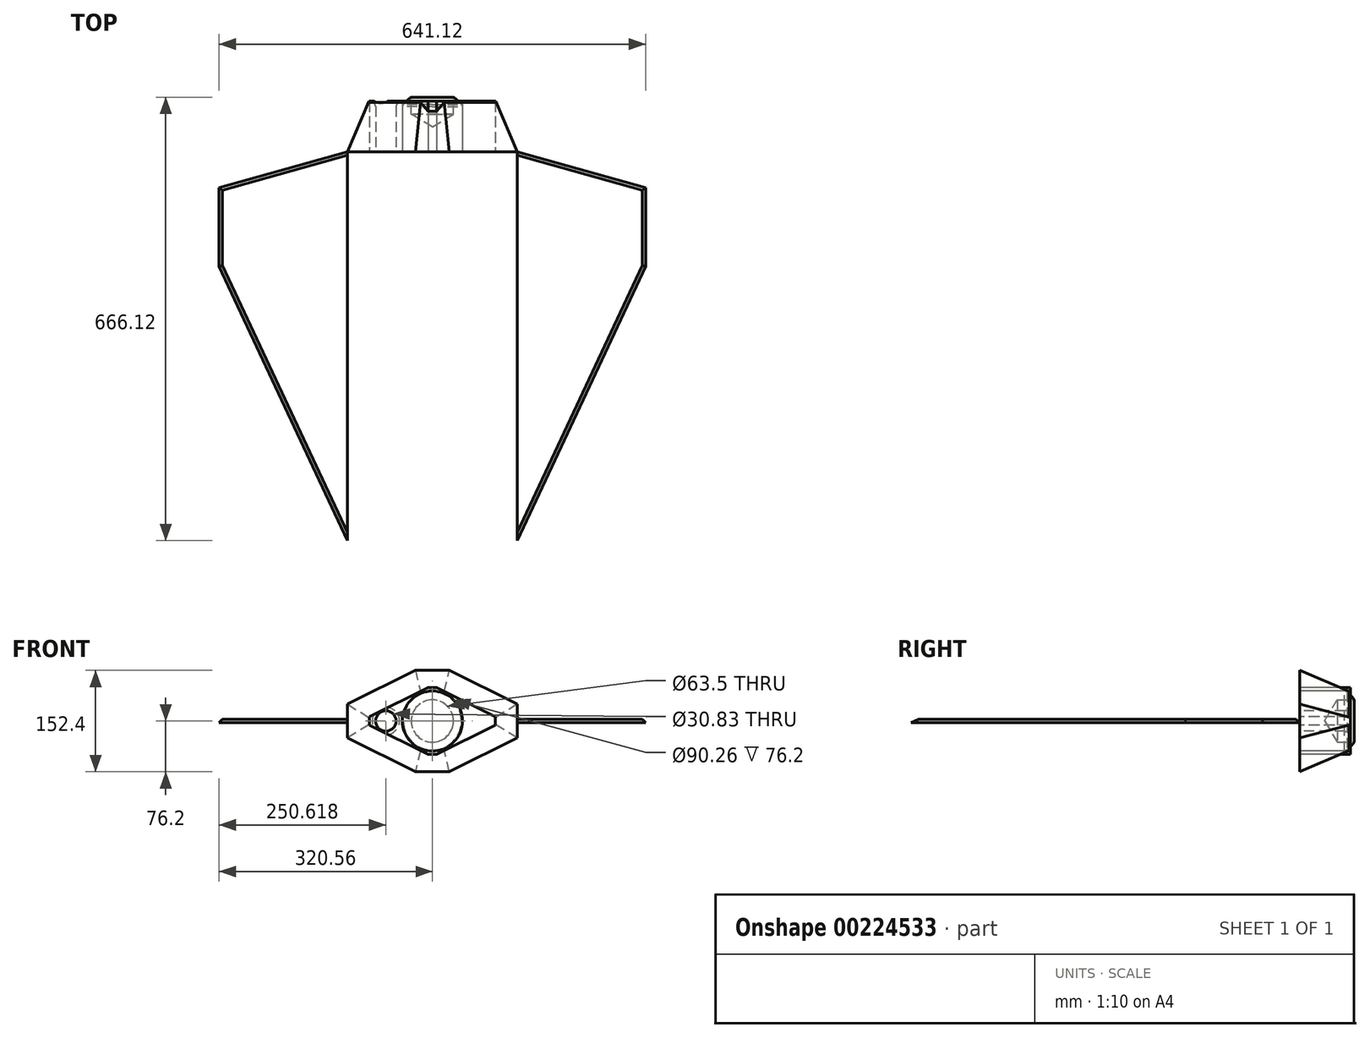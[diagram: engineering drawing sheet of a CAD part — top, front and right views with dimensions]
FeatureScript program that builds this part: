
annotation { "Feature Type Name" : "Feature", "Feature Type Description" : "" }
export const myFeature = defineFeature(function(context is Context, id is Id, definition is map)
    precondition{}
    {
        {
            var Q0;
            Q0=qCreatedBy(makeId("Top.planeOp"),FACE);
            var sketch = newSketch(context, id + "F0", { "sketchPlane" : qUnion([Q0])});
            skLineSegment(sketch, "E0", {"start": v(0, 0) * mm, "end": v(-127.58, 0) * mm});
            skLineSegment(sketch, "E1", {"start": v(0, 0) * mm, "end": v(0, -584.2) * mm});
            skLineSegment(sketch, "E2", {"start": v(0, -584.2) * mm, "end": v(-127.58, -584.2) * mm});
            skLineSegment(sketch, "E3", {"start": v(-127.58, -584.2) * mm, "end": v(-127.58, 0) * mm});
            skLineSegment(sketch, "E4", {"start": v(0, -584.2) * mm, "end": v(127.58, -584.2) * mm});
            skLineSegment(sketch, "E5", {"start": v(127.58, -584.2) * mm, "end": v(127.58, 0) * mm});
            skLineSegment(sketch, "E6", {"start": v(127.58, 0) * mm, "end": v(0, 0) * mm});
            skLineSegment(sketch, "E7", {"start": v(127.58, -584.2) * mm, "end": v(320.56, -172.08) * mm});
            skLineSegment(sketch, "E8", {"start": v(320.56, -172.08) * mm, "end": v(320.56, -53.88) * mm});
            skLineSegment(sketch, "E9", {"start": v(320.56, -53.88) * mm, "end": v(127.58, 0) * mm});
            skSolve(sketch);
        }
        {
            var Q0;
            Q0=makeQuery(id+"F0.imprint","IMPRINT",FACE,{"disambiguationData":[TD([[makeQuery(id+"F0.imprint","IMPRINT",EDGE,{"derivedFrom":sQuery(id+"F0.wireOp",EDGE,"E5")}),-1.0]])]});
            extrude(context, id + "F1", {"entities" : qUnion([Q0]), "depth" : 2.54 * mm, "hasSecondDirection" : true, "secondDirectionOppositeDirection" : true, "secondDirectionDepth" : 2.54 * mm});
        }
        {
            var Q0;
            Q0=makeQuery(id+"F1.opExtrude","CAP_EDGE",EDGE,{"disambiguationData":[OSD([sQuery(id+"F0.wireOp",EDGE,"E7")])],"isStart":false});
            var Q1;
            Q1=makeQuery(id+"F1.opExtrude","CAP_EDGE",EDGE,{"disambiguationData":[OSD([sQuery(id+"F0.wireOp",EDGE,"E8")])],"isStart":false});
            var Q2;
            Q2=makeQuery(id+"F1.opExtrude","CAP_EDGE",EDGE,{"disambiguationData":[OSD([sQuery(id+"F0.wireOp",EDGE,"E9")])],"isStart":false});
            chamfer(context, id + "F2", {"entities" : qUnion([Q0, Q1, Q2]), "width" : 5.08 * mm, "tangentPropagation" : true});
        }
        {
            var Q0;
            Q0=makeQuery(id+"F1.opExtrude","SWEPT_BODY",BODY,{"disambiguationData":[OSD([sQuery(id+"F0.wireOp",EDGE,"E5"),sQuery(id+"F0.wireOp",EDGE,"E7"),sQuery(id+"F0.wireOp",EDGE,"E8"),sQuery(id+"F0.wireOp",EDGE,"E9")])]});
            var Q1;
            Q1=qCreatedBy(makeId("Right.planeOp"),FACE);
            mirror(context, id + "F3", {"entities" : qUnion([Q0]), "mirrorPlane" : qUnion([Q1])});
        }
        {
            var Q0;
            Q0=qCreatedBy(makeId("Front.planeOp"),FACE);
            var sketch = newSketch(context, id + "F4", { "sketchPlane" : qUnion([Q0])});
            skLineSegment(sketch, "E10", {"start": v(-127.58, 0) * mm, "end": v(-127.58, 25.4) * mm});
            skLineSegment(sketch, "E11", {"start": v(0, 76.2) * mm, "end": v(-25.4, 76.2) * mm});
            skLineSegment(sketch, "E12", {"start": v(-25.4, 76.2) * mm, "end": v(-127.58, 25.4) * mm});
            skLineSegment(sketch, "E13.MirrorCS", {"start": v(-25.4, -76.2) * mm, "end": v(-127.58, -25.4) * mm});
            skLineSegment(sketch, "E14.MirrorCS", {"start": v(0, -76.2) * mm, "end": v(-25.4, -76.2) * mm});
            skLineSegment(sketch, "E15.MirrorCS", {"start": v(-127.58, 0) * mm, "end": v(-127.58, -25.4) * mm});
            skLineSegment(sketch, "E16.MirrorCS", {"start": v(0, 76.2) * mm, "end": v(25.4, 76.2) * mm});
            skLineSegment(sketch, "E17.MirrorCS", {"start": v(25.4, 76.2) * mm, "end": v(127.58, 25.4) * mm});
            skLineSegment(sketch, "E18.MirrorCS", {"start": v(127.58, 0) * mm, "end": v(127.58, -25.4) * mm});
            skLineSegment(sketch, "E19.MirrorCS", {"start": v(25.4, -76.2) * mm, "end": v(127.58, -25.4) * mm});
            skLineSegment(sketch, "E20.MirrorCS", {"start": v(0, -76.2) * mm, "end": v(25.4, -76.2) * mm});
            skLineSegment(sketch, "E21", {"start": v(94.75, 0) * mm, "end": v(94.75, 6.35) * mm});
            skLineSegment(sketch, "E22", {"start": v(94.75, 6.35) * mm, "end": v(6.35, 50.3) * mm});
            skLineSegment(sketch, "E23.MirrorCS", {"start": v(-94.75, 6.35) * mm, "end": v(-6.35, 50.3) * mm});
            skLineSegment(sketch, "E24.MirrorCS", {"start": v(94.75, -6.35) * mm, "end": v(6.35, -50.3) * mm});
            skLineSegment(sketch, "E25.MirrorCS", {"start": v(-94.75, -6.35) * mm, "end": v(-6.35, -50.3) * mm});
            skLineSegment(sketch, "E26", {"start": v(94.75, -6.35) * mm, "end": v(94.75, 6.35) * mm});
            skLineSegment(sketch, "E27", {"start": v(6.35, 50.3) * mm, "end": v(-6.35, 50.3) * mm});
            skLineSegment(sketch, "E28", {"start": v(-94.75, 6.35) * mm, "end": v(-94.75, -6.35) * mm});
            skLineSegment(sketch, "E29", {"start": v(-6.35, -50.3) * mm, "end": v(6.35, -50.3) * mm});
            skLineSegment(sketch, "E30", {"start": v(127.58, 25.4) * mm, "end": v(127.58, 0) * mm});
            skCircle(sketch, "E31", {"center": v(0, 0) * mm, "radius": 45.13 * mm});
            skLineSegment(sketch, "E32", {"start": v(94.75, 0) * mm, "end": v(45.13, 0) * mm});
            skCircle(sketch, "E33", {"center": v(69.94, 0) * mm, "radius": 15.42 * mm});
            skCircle(sketch, "E34.MirrorC", {"center": v(-69.94, 0) * mm, "radius": 15.42 * mm});
            skSolve(sketch);
        }
        {
            var Q0;
            Q0=makeQuery(id+"F4.imprint","IMPRINT",FACE,{"disambiguationData":[TD([[makeQuery(id+"F4.imprint","IMPRINT",EDGE,{"derivedFrom":sQuery(id+"F4.wireOp",EDGE,"E10")}),-1.0]])]});
            extrude(context, id + "F5", {"entities" : qUnion([Q0]), "oppositeDirection" : true, "depth" : 76.2 * mm});
        }
        {
            var Q0;
            Q0=makeQuery(id+"F5.opExtrude","CAP_EDGE",EDGE,{"disambiguationData":[OSD([sQuery(id+"F4.wireOp",EDGE,"E17.MirrorCS")])],"isStart":false});
            var Q1;
            Q1=makeQuery(id+"F5.opExtrude","CAP_EDGE",EDGE,{"disambiguationData":[OSD([sQuery(id+"F4.wireOp",EDGE,"E11"),sQuery(id+"F4.wireOp",EDGE,"E16.MirrorCS")])],"isStart":false});
            var Q2;
            Q2=makeQuery(id+"F5.opExtrude","CAP_EDGE",EDGE,{"disambiguationData":[OSD([sQuery(id+"F4.wireOp",EDGE,"E12")])],"isStart":false});
            var Q3;
            Q3=makeQuery(id+"F5.opExtrude","CAP_EDGE",EDGE,{"disambiguationData":[OSD([sQuery(id+"F4.wireOp",EDGE,"E10"),sQuery(id+"F4.wireOp",EDGE,"E15.MirrorCS")])],"isStart":false});
            var Q4;
            Q4=makeQuery(id+"F5.opExtrude","CAP_EDGE",EDGE,{"disambiguationData":[OSD([sQuery(id+"F4.wireOp",EDGE,"E13.MirrorCS")])],"isStart":false});
            var Q5;
            Q5=makeQuery(id+"F5.opExtrude","CAP_EDGE",EDGE,{"disambiguationData":[OSD([sQuery(id+"F4.wireOp",EDGE,"E14.MirrorCS"),sQuery(id+"F4.wireOp",EDGE,"E20.MirrorCS")])],"isStart":false});
            var Q6;
            Q6=makeQuery(id+"F5.opExtrude","CAP_EDGE",EDGE,{"disambiguationData":[OSD([sQuery(id+"F4.wireOp",EDGE,"E19.MirrorCS")])],"isStart":false});
            var Q7;
            Q7=makeQuery(id+"F5.opExtrude","CAP_EDGE",EDGE,{"disambiguationData":[OSD([sQuery(id+"F4.wireOp",EDGE,"E18.MirrorCS"),sQuery(id+"F4.wireOp",EDGE,"E30")])],"isStart":false});
            chamfer(context, id + "F6", {"entities" : qUnion([Q0, Q1, Q2, Q3, Q4, Q5, Q6, Q7]), "chamferType" : ChamferType.OFFSET_ANGLE, "width" : 76.2 * mm, "oppositeDirection" : true, "angle" : 23 * degree, "tangentPropagation" : true});
        }
        {
            var Q0;
            Q0=makeQuery(id+"F4.imprint","IMPRINT",FACE,{"disambiguationData":[TD([[makeQuery(id+"F4.imprint","IMPRINT",EDGE,{"derivedFrom":sQuery(id+"F4.wireOp",EDGE,"E31")}),1.0]])]});
            extrude(context, id + "F7", {"entities" : qUnion([Q0]), "oppositeDirection" : true, "depth" : 82.55 * mm});
        }
        {
            var Q0;
            {var subQ0=sQuery(id+"F4.wireOp",EDGE,"E33");var subQ1=sQuery(id+"F4.wireOp",EDGE,"E32");var subQ2=makeQuery(id+"F4.imprint","INTERSECT",VERTEX,{"disambiguationData":[OD(0.0)],"derivedFrom":[subQ1,subQ0]});Q0=makeQuery(id+"F4.imprint","IMPRINT",FACE,{"disambiguationData":[TD([[makeQuery(id+"F4.imprint","IMPRINT",EDGE,{"disambiguationData":[TD([[subQ2,1.0]])],"derivedFrom":subQ1}),-1.0]])]});}
            var Q1;
            {var subQ0=sQuery(id+"F4.wireOp",EDGE,"E33");var subQ1=sQuery(id+"F4.wireOp",EDGE,"E32");var subQ2=makeQuery(id+"F4.imprint","INTERSECT",VERTEX,{"disambiguationData":[OD(0.0)],"derivedFrom":[subQ1,subQ0]});Q1=makeQuery(id+"F4.imprint","IMPRINT",FACE,{"disambiguationData":[TD([[makeQuery(id+"F4.imprint","IMPRINT",EDGE,{"disambiguationData":[TD([[subQ2,1.0]])],"derivedFrom":subQ1}),1.0]])]});}
            var Q2;
            Q2=makeQuery(id+"F4.imprint","IMPRINT",FACE,{"disambiguationData":[TD([[makeQuery(id+"F4.imprint","IMPRINT",EDGE,{"derivedFrom":sQuery(id+"F4.wireOp",EDGE,"E34.MirrorC")}),-1.0]])]});
            extrude(context, id + "F8", {"entities" : qUnion([Q0, Q1, Q2]), "oppositeDirection" : true, "depth" : 76.2 * mm});
        }
        {
            var Q0;
            Q0=makeQuery(id+"F7.opExtrude","CAP_EDGE",EDGE,{"disambiguationData":[OSD([sQuery(id+"F4.wireOp",EDGE,"E31")])],"isStart":false});
            chamfer(context, id + "F9", {"entities" : qUnion([Q0]), "width" : 12.7 * mm, "tangentPropagation" : true});
        }
        {
            var Q0;
            {var subQ0=sQuery(id+"F4.wireOp",EDGE,"E31");Q0=makeQuery(id+"F9.opChamfer","BLEND_EDGE",EDGE,{"blendedFrom":[makeQuery(id+"F7.opExtrude","CAP_EDGE",EDGE,{"disambiguationData":[OSD([subQ0])],"isStart":false}),makeQuery(id+"F7.opExtrude","CAP_FACE",FACE,{"disambiguationData":[OSD([subQ0])],"isStart":false})],"blendedInto":[makeQuery(id+"F7.opExtrude","CAP_FACE",FACE,{"disambiguationData":[OSD([subQ0])],"isStart":false})]});}
            fillet(context, id + "F10", {"entities" : qUnion([Q0]), "radius" : 10.16 * mm, "tangentPropagation" : true, "allowEdgeOverflow" : false});
        }
        {
            var Q0;
            Q0=makeQuery(id+"F7.opExtrude","CAP_FACE",FACE,{"disambiguationData":[OSD([sQuery(id+"F4.wireOp",EDGE,"E31")])],"isStart":false});
            var sketch = newSketch(context, id + "F11", { "sketchPlane" : qUnion([Q0])});
            skPoint(sketch, "E35", {"position": v(0, 0) * mm});
            skSolve(sketch);
        }
        {
            var Q0;
            Q0=sQuery(id+"F11.wireOp",VERTEX,"E35");
            var Q1;
            Q1=makeQuery(id+"F7.opExtrude","SWEPT_BODY",BODY,{"disambiguationData":[OSD([sQuery(id+"F4.wireOp",EDGE,"E31")])]});
            hole(context, id + "F12", {"style" : HoleStyle.SIMPLE, "endStyle" : HoleEndStyle.BLIND, "holeDiameter" : 63.5 * mm, "holeDepth" : 25.4 * mm, "locations" : qUnion([Q0]), "scope" : qUnion([Q1])});
        }
        {
            var Q0;
            {var subQ0=sQuery(id+"F4.wireOp",EDGE,"E31");Q0=makeQuery(id+"F9.opChamfer","BLEND_EDGE",EDGE,{"blendedFrom":[makeQuery(id+"F7.opExtrude","CAP_EDGE",EDGE,{"disambiguationData":[OSD([subQ0])],"isStart":false}),makeQuery(id+"F7.opExtrude","SWEPT_FACE",FACE,{"disambiguationData":[OSD([subQ0])]})],"blendedInto":[makeQuery(id+"F7.opExtrude","SWEPT_FACE",FACE,{"disambiguationData":[OSD([subQ0])]})]});}
            chamfer(context, id + "F13", {"entities" : qUnion([Q0]), "width" : 5.08 * mm, "tangentPropagation" : true});
        }
        {
            var Q0;
            Q0=makeQuery(id+"F8.opExtrude","CAP_EDGE",EDGE,{"disambiguationData":[OSD([sQuery(id+"F4.wireOp",EDGE,"E33")])],"isStart":false});
            var Q1;
            Q1=makeQuery(id+"F8.opExtrude","CAP_EDGE",EDGE,{"disambiguationData":[OSD([sQuery(id+"F4.wireOp",EDGE,"E34.MirrorC")])],"isStart":false});
            chamfer(context, id + "F14", {"entities" : qUnion([Q0, Q1]), "width" : 5.08 * mm, "tangentPropagation" : true});
        }
        {
            var Q0;
            {var subQ0=sQuery(id+"F4.wireOp",EDGE,"E33");Q0=makeQuery(id+"F14.opChamfer","BLEND_EDGE",EDGE,{"blendedFrom":[makeQuery(id+"F8.opExtrude","CAP_EDGE",EDGE,{"disambiguationData":[OSD([subQ0])],"isStart":false}),makeQuery(id+"F8.opExtrude","SWEPT_FACE",FACE,{"disambiguationData":[OSD([subQ0])]})],"blendedInto":[makeQuery(id+"F8.opExtrude","SWEPT_FACE",FACE,{"disambiguationData":[OSD([subQ0])]})]});}
            var Q1;
            {var subQ0=sQuery(id+"F4.wireOp",EDGE,"E34.MirrorC");Q1=makeQuery(id+"F14.opChamfer","BLEND_EDGE",EDGE,{"blendedFrom":[makeQuery(id+"F8.opExtrude","CAP_EDGE",EDGE,{"disambiguationData":[OSD([subQ0])],"isStart":false}),makeQuery(id+"F8.opExtrude","SWEPT_FACE",FACE,{"disambiguationData":[OSD([subQ0])]})],"blendedInto":[makeQuery(id+"F8.opExtrude","SWEPT_FACE",FACE,{"disambiguationData":[OSD([subQ0])]})]});}
            fillet(context, id + "F15", {"entities" : qUnion([Q0, Q1]), "radius" : 7.62 * mm, "tangentPropagation" : true, "allowEdgeOverflow" : false});
        }
        {
            var Q0;
            Q0=makeQuery(id+"F8.opExtrude","CAP_FACE",FACE,{"disambiguationData":[OSD([sQuery(id+"F4.wireOp",EDGE,"E33")])],"isStart":false});
            var sketch = newSketch(context, id + "F16", { "sketchPlane" : qUnion([Q0])});
            skPoint(sketch, "E36", {"position": v(-69.94, 0) * mm});
            skSolve(sketch);
        }
        {
            var Q0;
            Q0=makeQuery(id+"F8.opExtrude","CAP_FACE",FACE,{"disambiguationData":[OSD([sQuery(id+"F4.wireOp",EDGE,"E34.MirrorC")])],"isStart":false});
            var sketch = newSketch(context, id + "F17", { "sketchPlane" : qUnion([Q0])});
            skPoint(sketch, "E37", {"position": v(69.94, 0) * mm});
            skSolve(sketch);
        }
        {
            var Q0;
            Q0=sQuery(id+"F16.wireOp",VERTEX,"E36");
            var Q1;
            Q1=sQuery(id+"F17.wireOp",VERTEX,"E37");
            var Q2;
            Q2=makeQuery(id+"F8.opExtrude","SWEPT_BODY",BODY,{"disambiguationData":[OSD([sQuery(id+"F4.wireOp",EDGE,"E33")])]});
            var Q3;
            Q3=makeQuery(id+"F8.opExtrude","SWEPT_BODY",BODY,{"disambiguationData":[OSD([sQuery(id+"F4.wireOp",EDGE,"E34.MirrorC")])]});
            hole(context, id + "F18", {"style" : HoleStyle.SIMPLE, "endStyle" : HoleEndStyle.BLIND, "holeDiameter" : 19.05 * mm, "holeDepth" : 19.05 * mm, "locations" : qUnion([Q0, Q1]), "scope" : qUnion([Q2, Q3])});
        }
    });
